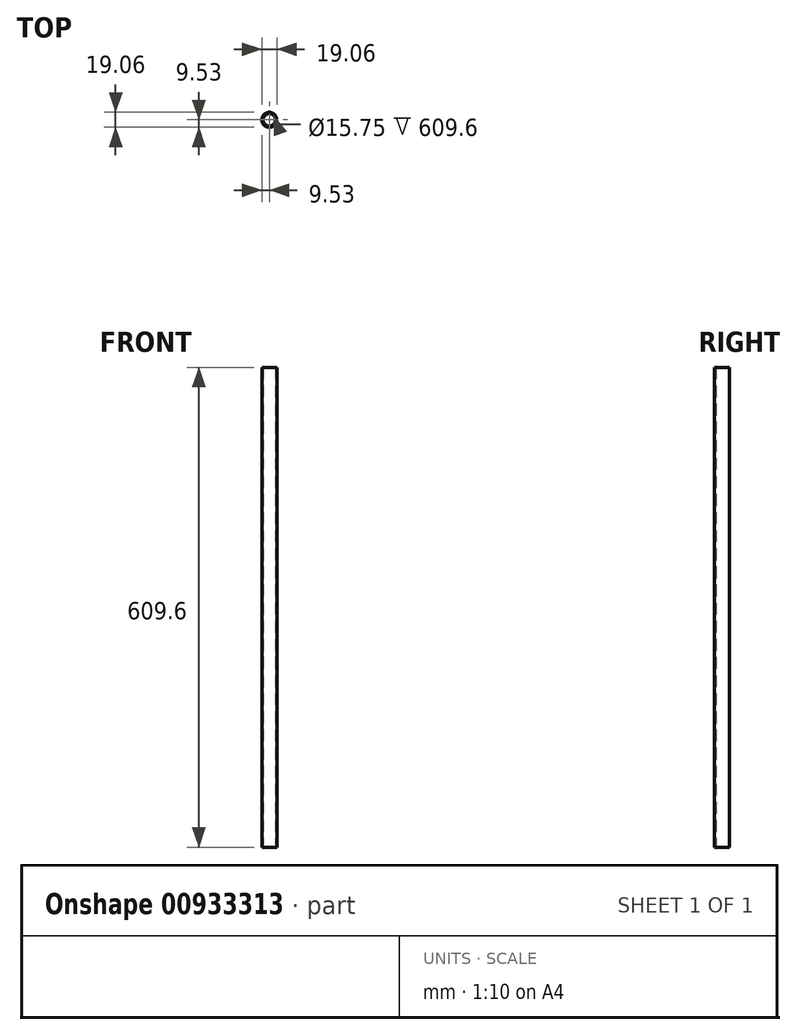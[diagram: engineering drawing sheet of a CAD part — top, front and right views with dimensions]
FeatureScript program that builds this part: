
annotation { "Feature Type Name" : "Feature", "Feature Type Description" : "" }
export const myFeature = defineFeature(function(context is Context, id is Id, definition is map)
    precondition{}
    {
        {
            var Q0;
            Q0=qCreatedBy(makeId("Top.planeOp"),FACE);
            var sketch = newSketch(context, id + "F0", { "sketchPlane" : qUnion([Q0])});
            skCircle(sketch, "E0", {"center": v(0, 0) * mm, "radius": 9.53 * mm});
            skCircle(sketch, "E1", {"center": v(0, 0) * mm, "radius": 7.87 * mm});
            skSolve(sketch);
        }
        {
            var Q0;
            Q0=makeQuery(id+"F0.imprint","IMPRINT",FACE,{"disambiguationData":[TD([[makeQuery(id+"F0.imprint","IMPRINT",EDGE,{"derivedFrom":sQuery(id+"F0.wireOp",EDGE,"E0")}),1.0]])]});
            extrude(context, id + "F1", {"entities" : qUnion([Q0]), "depth" : 609.6 * mm, "offsetDistance" : 25.4 * mm});
        }
    });
